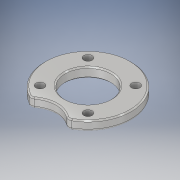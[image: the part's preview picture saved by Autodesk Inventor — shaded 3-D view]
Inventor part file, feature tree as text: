
AUTODESK INVENTOR PART (.ipt)
format: ipt  version: 2019.4 (Build 234330000, 330)  size: 205,824 bytes
history: native  units: mm
features: fillet x2, chamfer x2, extrude x1, sketch x1
ambient origin geometry x8: Origin, YZ Plane, XZ Plane, XY Plane, X Axis, Y Axis, Z Axis, Center Point
bodies: Solid1 (feature_tree)
feature tree (6):
  extrude  "Extrusion1"  Depth=3.75mm
  fillet  "Fillet1"  Radius=40.0mm
  fillet  "Fillet2"  [1 undecoded]
  chamfer  "Chamfer1"  Distance=20.0mm
  chamfer  "Chamfer2"  Distance=15.0mm
  sketch  "Sketch1"  dims[d0=18.5mm d2=3.4mm d4=40.0mm d6=360.0deg d8=45.0deg d10=20.0mm d11=15.0mm d12=4.0mm d13=0.0mm d14=2.0mm d15=1.0mm d24=0.5mm d25=2.0mm d26=45.0deg d27=0.0mm d30=7.5mm d31=3.75mm d32=0.5mm d33=2.0mm d34=45.0deg]
note: 1 required parameter value undecoded (feature->parameter linkage not recoverable at this tier; creation-order binding heuristic only, values carry confidence <= 0.55)
